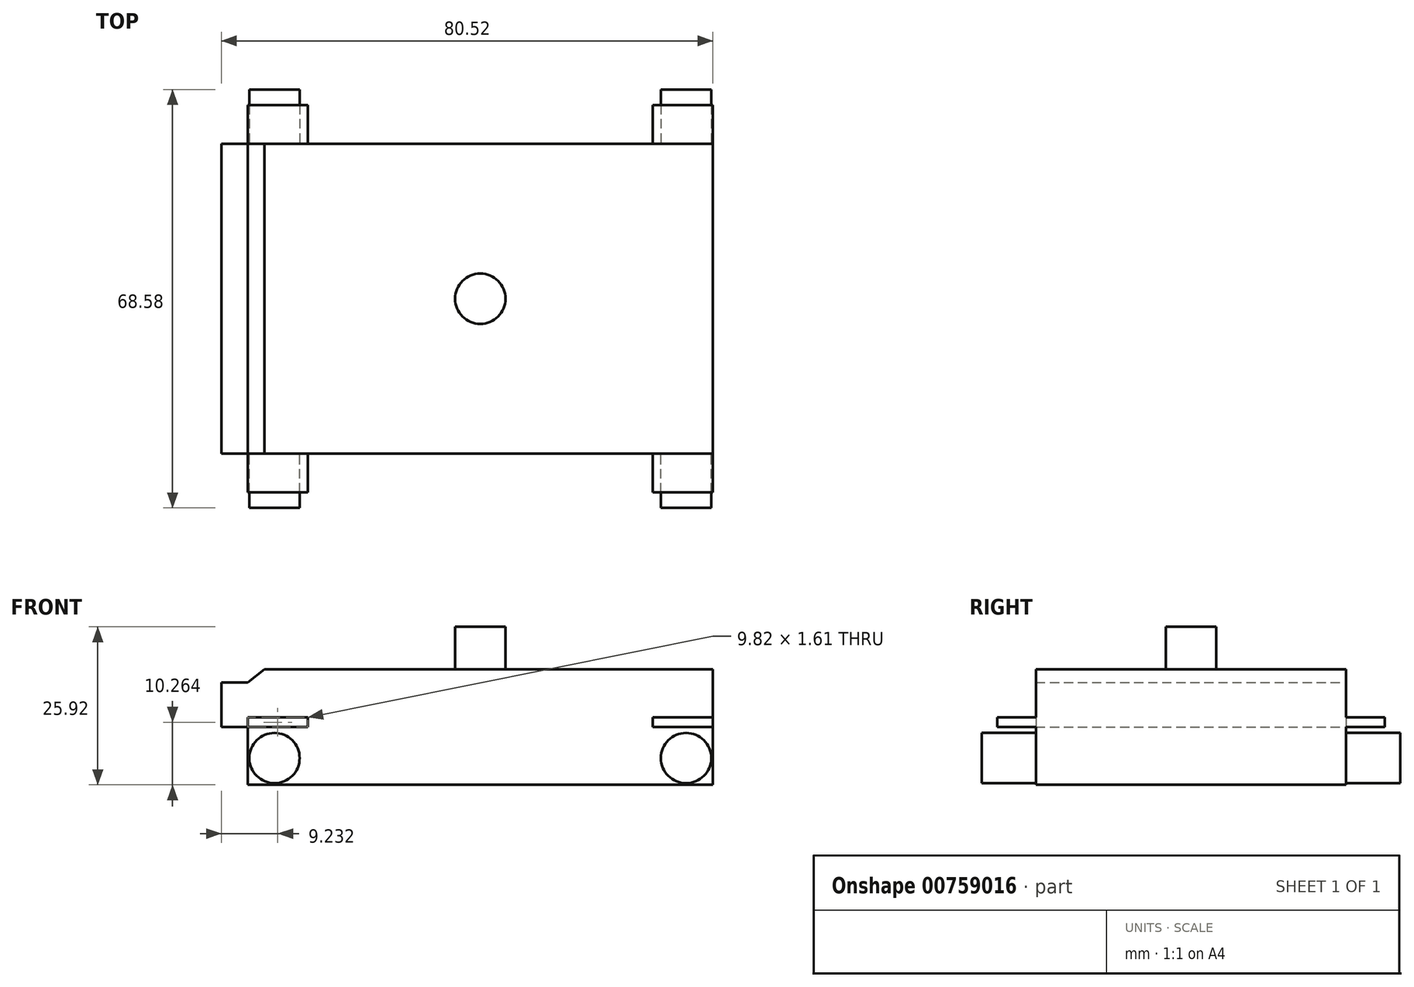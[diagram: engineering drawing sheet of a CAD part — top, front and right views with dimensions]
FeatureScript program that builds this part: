
annotation { "Feature Type Name" : "Feature", "Feature Type Description" : "" }
export const myFeature = defineFeature(function(context is Context, id is Id, definition is map)
    precondition{}
    {
        {
            var Q0;
            Q0=qCreatedBy(makeId("Front.planeOp"),FACE);
            var sketch = newSketch(context, id + "F0", { "sketchPlane" : qUnion([Q0])});
            skLineSegment(sketch, "E0.bottom", {"start": v(-38.1, 9.46) * mm, "end": v(38.1, 9.46) * mm});
            skLineSegment(sketch, "E0.top", {"start": v(-38.1, -9.46) * mm, "end": v(38.1, -9.46) * mm});
            skLineSegment(sketch, "E0.left", {"start": v(-38.1, 9.46) * mm, "end": v(-38.1, -9.46) * mm});
            skLineSegment(sketch, "E0.right", {"start": v(38.1, 9.46) * mm, "end": v(38.1, -9.46) * mm});
            skPoint(sketch, "E0.middle", {"position": v(0, 0) * mm});
            skLineSegment(sketch, "E1", {"start": v(-38.1, 0) * mm, "end": v(-28.28, 0) * mm});
            skLineSegment(sketch, "E2", {"start": v(-28.28, 0) * mm, "end": v(-28.28, -9.46) * mm});
            skLineSegment(sketch, "E3", {"start": v(-38.1, 1.6) * mm, "end": v(-28.28, 1.6) * mm});
            skLineSegment(sketch, "E4", {"start": v(-28.28, 1.6) * mm, "end": v(-28.28, 0) * mm});
            skLineSegment(sketch, "E5", {"start": v(-38.1, 7.36) * mm, "end": v(-35.37, 9.46) * mm});
            skLineSegment(sketch, "E6.MirrorCS", {"start": v(38.1, 0) * mm, "end": v(28.28, 0) * mm});
            skLineSegment(sketch, "E7.MirrorCS", {"start": v(38.1, 1.6) * mm, "end": v(28.28, 1.6) * mm});
            skLineSegment(sketch, "E8.MirrorCS", {"start": v(28.28, 0) * mm, "end": v(28.28, -9.46) * mm});
            skLineSegment(sketch, "E9.MirrorCS", {"start": v(28.28, 1.6) * mm, "end": v(28.28, 0) * mm});
            skSolve(sketch);
        }
        {
            var Q0;
            {var subQ3=sQuery(id+"F0.wireOp",EDGE,"E2");Q0=makeQuery(id+"F0.imprint","IMPRINT",FACE,{"disambiguationData":[TD([[makeQuery(id+"F0.imprint","IMPRINT",EDGE,{"derivedFrom":subQ3}),1.0]])]});}
            extrude(context, id + "F1", {"entities" : qUnion([Q0]), "endBound" : BoundingType.SYMMETRIC, "depth" : 50.8 * mm, "offsetDistance" : 25.4 * mm});
        }
        {
            var Q0;
            {var subQ0=sQuery(id+"F0.wireOp",EDGE,"E1");Q0=makeQuery(id+"F0.imprint","IMPRINT",FACE,{"disambiguationData":[TD([[makeQuery(id+"F0.imprint","IMPRINT",EDGE,{"derivedFrom":subQ0}),1.0]])]});}
            var Q1;
            {var subQ0=sQuery(id+"F0.wireOp",EDGE,"E6.MirrorCS");Q1=makeQuery(id+"F0.imprint","IMPRINT",FACE,{"disambiguationData":[TD([[makeQuery(id+"F0.imprint","IMPRINT",EDGE,{"derivedFrom":subQ0}),-1.0]])]});}
            extrude(context, id + "F2", {"entities" : qUnion([Q0, Q1]), "operationType" : NewBodyOperationType.ADD, "endBound" : BoundingType.SYMMETRIC, "depth" : 63.5 * mm, "offsetDistance" : 25.4 * mm});
        }
        {
            var Q0;
            {var subQ4=sQuery(id+"F0.wireOp",EDGE,"E1");Q0=makeQuery(id+"F0.imprint","IMPRINT",FACE,{"disambiguationData":[TD([[makeQuery(id+"F0.imprint","IMPRINT",EDGE,{"derivedFrom":subQ4}),-1.0]])]});}
            var Q1;
            {var subQ4=sQuery(id+"F0.wireOp",EDGE,"E6.MirrorCS");Q1=makeQuery(id+"F0.imprint","IMPRINT",FACE,{"disambiguationData":[TD([[makeQuery(id+"F0.imprint","IMPRINT",EDGE,{"derivedFrom":subQ4}),1.0]])]});}
            extrude(context, id + "F3", {"entities" : qUnion([Q0, Q1]), "operationType" : NewBodyOperationType.ADD, "endBound" : BoundingType.SYMMETRIC, "depth" : 38.1 * mm, "offsetDistance" : 25.4 * mm});
        }
        {
            var Q0;
            {var subQ0=sQuery(id+"F0.wireOp",EDGE,"E0.left");Q0=makeQuery(id+"F3.boolean.opBoolean","MERGE",FACE,{"derivedFrom":[makeQuery(id+"F2.boolean.opBoolean","MERGE",FACE,{"derivedFrom":[makeQuery(id+"F1.opExtrude","SWEPT_FACE",FACE,{"disambiguationData":[OSD([subQ0])]}),makeQuery(id+"F2.opExtrude","SWEPT_FACE",FACE,{"disambiguationData":[OSD([subQ0])]})]}),makeQuery(id+"F3.opExtrude","SWEPT_FACE",FACE,{"disambiguationData":[OSD([subQ0])]})]});}
            var sketch = newSketch(context, id + "F4", { "sketchPlane" : qUnion([Q0])});
            skLineSegment(sketch, "E10", {"start": v(19.05, 0) * mm, "end": v(-19.05, 0) * mm});
            skLineSegment(sketch, "E11", {"start": v(-25.4, 1.6) * mm, "end": v(-25.4, 0) * mm});
            skLineSegment(sketch, "E12", {"start": v(25.4, 1.6) * mm, "end": v(25.4, 0) * mm});
            skSolve(sketch);
        }
        {
            var Q0;
            {var subQ1=sQuery(id+"F4.wireOp",EDGE,"E10");Q0=makeQuery(id+"F4.imprint","IMPRINT",FACE,{"disambiguationData":[TD([[makeQuery(id+"F4.imprint","IMPRINT",EDGE,{"derivedFrom":subQ1}),-1.0]])]});}
            extrude(context, id + "F5", {"entities" : qUnion([Q0]), "operationType" : NewBodyOperationType.ADD, "depth" : 4.32 * mm, "offsetDistance" : 25.4 * mm});
        }
        {
            var Q0;
            Q0=makeQuery(id+"F3.opExtrude","CAP_FACE",FACE,{"disambiguationData":[OSD([sQuery(id+"F0.wireOp",EDGE,"E0.top"),sQuery(id+"F0.wireOp",EDGE,"E0.left"),sQuery(id+"F0.wireOp",EDGE,"E1"),sQuery(id+"F0.wireOp",EDGE,"E2")])],"isStart":false});
            var sketch = newSketch(context, id + "F6", { "sketchPlane" : qUnion([Q0])});
            skCircle(sketch, "E13", {"center": v(-33.72, -5.08) * mm, "radius": 4.12 * mm});
            skSolve(sketch);
        }
        {
            var Q0;
            Q0=makeQuery(id+"F3.opExtrude","CAP_FACE",FACE,{"disambiguationData":[OSD([sQuery(id+"F0.wireOp",EDGE,"E0.top"),sQuery(id+"F0.wireOp",EDGE,"E0.left"),sQuery(id+"F0.wireOp",EDGE,"E1"),sQuery(id+"F0.wireOp",EDGE,"E2")])],"isStart":true});
            var sketch = newSketch(context, id + "F7", { "sketchPlane" : qUnion([Q0])});
            skCircle(sketch, "E14", {"center": v(33.72, -5.08) * mm, "radius": 4.12 * mm});
            skSolve(sketch);
        }
        {
            var Q0;
            Q0=makeQuery(id+"F1.opExtrude","SWEPT_FACE",FACE,{"disambiguationData":[OSD([sQuery(id+"F0.wireOp",EDGE,"E0.bottom")])]});
            var sketch = newSketch(context, id + "F8", { "sketchPlane" : qUnion([Q0])});
            skCircle(sketch, "E15", {"center": v(0, 0) * mm, "radius": 4.12 * mm});
            skSolve(sketch);
        }
        {
            var Q0;
            Q0=makeQuery(id+"F8.imprint","IMPRINT",FACE,{"disambiguationData":[TD([[makeQuery(id+"F8.imprint","IMPRINT",EDGE,{"derivedFrom":sQuery(id+"F8.wireOp",EDGE,"E15")}),1.0]])]});
            extrude(context, id + "F9", {"entities" : qUnion([Q0]), "operationType" : NewBodyOperationType.ADD, "depth" : 7 * mm, "offsetDistance" : 25.4 * mm});
        }
        {
            var Q0;
            Q0=makeQuery(id+"F3.opExtrude","CAP_FACE",FACE,{"disambiguationData":[OSD([sQuery(id+"F0.wireOp",EDGE,"E0.top"),sQuery(id+"F0.wireOp",EDGE,"E0.right"),sQuery(id+"F0.wireOp",EDGE,"E6.MirrorCS"),sQuery(id+"F0.wireOp",EDGE,"E8.MirrorCS")])],"isStart":false});
            var sketch = newSketch(context, id + "F10", { "sketchPlane" : qUnion([Q0])});
            skCircle(sketch, "E16", {"center": v(33.72, -5.08) * mm, "radius": 4.12 * mm});
            skSolve(sketch);
        }
        {
            var Q0;
            Q0=makeQuery(id+"F3.opExtrude","CAP_FACE",FACE,{"disambiguationData":[OSD([sQuery(id+"F0.wireOp",EDGE,"E0.top"),sQuery(id+"F0.wireOp",EDGE,"E0.right"),sQuery(id+"F0.wireOp",EDGE,"E6.MirrorCS"),sQuery(id+"F0.wireOp",EDGE,"E8.MirrorCS")])],"isStart":true});
            var sketch = newSketch(context, id + "F11", { "sketchPlane" : qUnion([Q0])});
            skCircle(sketch, "E17", {"center": v(-33.72, -5.08) * mm, "radius": 4.12 * mm});
            skSolve(sketch);
        }
        {
            var Q0;
            Q0=makeQuery(id+"F11.imprint","IMPRINT",FACE,{"disambiguationData":[TD([[makeQuery(id+"F11.imprint","IMPRINT",EDGE,{"derivedFrom":sQuery(id+"F11.wireOp",EDGE,"E17")}),1.0]])]});
            var Q1;
            Q1=makeQuery(id+"F7.imprint","IMPRINT",FACE,{"disambiguationData":[TD([[makeQuery(id+"F7.imprint","IMPRINT",EDGE,{"derivedFrom":sQuery(id+"F7.wireOp",EDGE,"E14")}),1.0]])]});
            extrude(context, id + "F12", {"entities" : qUnion([Q0, Q1]), "operationType" : NewBodyOperationType.ADD, "depth" : 15.24 * mm, "offsetDistance" : 25.4 * mm});
        }
        {
            var Q0;
            Q0=makeQuery(id+"F6.imprint","IMPRINT",FACE,{"disambiguationData":[TD([[makeQuery(id+"F6.imprint","IMPRINT",EDGE,{"derivedFrom":sQuery(id+"F6.wireOp",EDGE,"E13")}),1.0]])]});
            var Q1;
            Q1=makeQuery(id+"F10.imprint","IMPRINT",FACE,{"disambiguationData":[TD([[makeQuery(id+"F10.imprint","IMPRINT",EDGE,{"derivedFrom":sQuery(id+"F10.wireOp",EDGE,"E16")}),1.0]])]});
            extrude(context, id + "F13", {"entities" : qUnion([Q0, Q1]), "operationType" : NewBodyOperationType.ADD, "depth" : 15.24 * mm, "offsetDistance" : 25.4 * mm});
        }
        {
            var Q0;
            Q0=makeQuery(id+"F3.opExtrude","CAP_FACE",FACE,{"disambiguationData":[OSD([sQuery(id+"F0.wireOp",EDGE,"E0.top"),sQuery(id+"F0.wireOp",EDGE,"E0.left"),sQuery(id+"F0.wireOp",EDGE,"E1"),sQuery(id+"F0.wireOp",EDGE,"E2")])],"isStart":false});
            var Q1;
            Q1=makeQuery(id+"F3.opExtrude","CAP_FACE",FACE,{"disambiguationData":[OSD([sQuery(id+"F0.wireOp",EDGE,"E0.top"),sQuery(id+"F0.wireOp",EDGE,"E0.right"),sQuery(id+"F0.wireOp",EDGE,"E6.MirrorCS"),sQuery(id+"F0.wireOp",EDGE,"E8.MirrorCS")])],"isStart":false});
            extrude(context, id + "F14", {"entities" : qUnion([Q0, Q1]), "operationType" : NewBodyOperationType.ADD, "depth" : 6.35 * mm, "offsetDistance" : 25.4 * mm});
        }
        {
            var Q0;
            Q0=makeQuery(id+"F3.opExtrude","CAP_FACE",FACE,{"disambiguationData":[OSD([sQuery(id+"F0.wireOp",EDGE,"E0.top"),sQuery(id+"F0.wireOp",EDGE,"E0.right"),sQuery(id+"F0.wireOp",EDGE,"E6.MirrorCS"),sQuery(id+"F0.wireOp",EDGE,"E8.MirrorCS")])],"isStart":true});
            var Q1;
            Q1=makeQuery(id+"F3.opExtrude","CAP_FACE",FACE,{"disambiguationData":[OSD([sQuery(id+"F0.wireOp",EDGE,"E0.top"),sQuery(id+"F0.wireOp",EDGE,"E0.left"),sQuery(id+"F0.wireOp",EDGE,"E1"),sQuery(id+"F0.wireOp",EDGE,"E2")])],"isStart":true});
            extrude(context, id + "F15", {"entities" : qUnion([Q0, Q1]), "operationType" : NewBodyOperationType.ADD, "depth" : 6.35 * mm, "offsetDistance" : 25.4 * mm});
        }
    });
